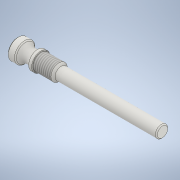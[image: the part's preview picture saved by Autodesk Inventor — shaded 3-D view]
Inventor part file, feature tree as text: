
AUTODESK INVENTOR PART (.ipt)
format: ipt  version: 2020 (Build 240168000, 168)  size: 145,408 bytes
history: native  units: mm
features: revolve x2, chamfer x2, other x2, fillet x1, thread x1, sketch x1, projected_geometry x1
ambient origin geometry x6: Origin, XZ Plane, XY Plane, X Axis, Y Axis, Z Axis
bodies: 实体1 (feature_tree)
feature tree (10):
  revolve  "旋转1"  [1 undecoded]
  chamfer  "倒角1"  Distance=18.0mm
  fillet  "圆角1"  Radius=16.0mm
  chamfer  "倒角2"  Distance=12.0mm
  thread  "螺纹1"  [1 undecoded]
  revolve  "旋转2"  Angle=45.0deg
  other  "起始平面"
  other  "主草图"
  sketch  "草图3"  dims[d0=0.0mm d1=0.0mm d2=0.0mm d3=20.0mm d4=18.0mm d5=16.0mm d6=12.0mm d7=0.0mm d8=1.0mm d9=2.0mm d10=45.0deg d11=1.0mm d12=2.0mm d13=2.0mm d14=45.0deg d15=23.0mm d16=0.0mm d17=3.0mm d18=8.0mm d19=90.0deg]
  projected_geometry  "投影回路1"
note: 2 required parameter values undecoded (feature->parameter linkage not recoverable at this tier; creation-order binding heuristic only, values carry confidence <= 0.55)